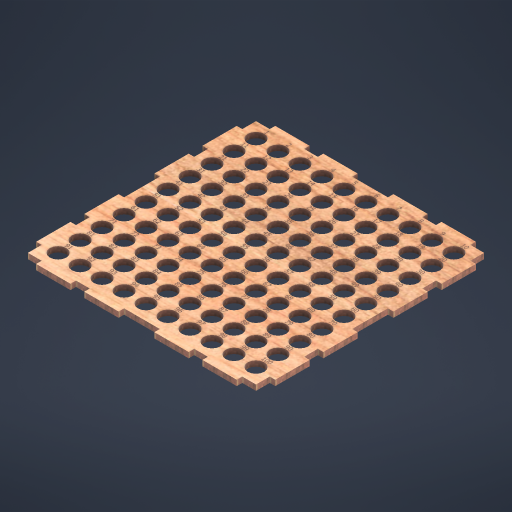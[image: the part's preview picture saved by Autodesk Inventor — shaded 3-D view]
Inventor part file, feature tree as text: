
AUTODESK INVENTOR PART (.ipt)
format: ipt  version: 2024.1 (Build 281209000, 209)  size: 8,317,440 bytes
history: native  units: mm
features: extrude x2, sketch x2, projected_geometry x1
ambient origin geometry x8: Origin, YZ Plane, XZ Plane, XY Plane, X Axis, Y Axis, Z Axis, Center Point
bodies: Solid1 (feature_tree)
feature tree (5):
  extrude  "Extrusion1"  Depth=100.0mm
  extrude  "Extrusion2"  Depth=5.0mm
  sketch  "Sketch1"  dims[d0=12.0mm d1=100.0mm d3=16.0mm]
  sketch  "Sketch2"  dims[d4=100.0mm d6=16.0mm d9=5.0mm d10=5.0mm d11=4.0mm d12=4.0mm d13=10.0mm d14=10.0mm d15=25.0mm d16=4.0mm d17=25.0mm d18=10.0mm d19=25.0mm d20=10.0mm d21=25.0mm d22=4.0mm d23=40.0mm d25=360.0deg d27=4.0mm d28=0.0mm d29=3.0mm d30=0.5mm d31=16.0mm d32=4.0mm d33=3.0mm d34=4.0mm d35=3.0mm d36=4.0mm d37=3.0mm d38=4.0mm d39=3.0mm d40=4.0mm d41=3.0mm d42=4.0mm d43=3.0mm d44=4.0mm d45=3.0mm d46=4.0mm d47=3.0mm d48=4.0mm d49=3.0mm d50=4.0mm d51=3.0mm d52=4.0mm d53=3.0mm d54=4.0mm d55=3.0mm d56=4.0mm d57=3.0mm d58=4.0mm d59=3.0mm d60=4.0mm d61=3.0mm d62=4.0mm d63=3.0mm d64=4.0mm d65=3.0mm d66=4.0mm d67=3.0mm d68=4.0mm d69=3.0mm d70=4.0mm d71=3.0mm d72=4.0mm d73=3.0mm d74=4.0mm d75=3.0mm d76=4.0mm d77=3.0mm d78=4.0mm d79=3.0mm d80=4.0mm d81=3.0mm d82=4.0mm d83=3.0mm d84=4.0mm d85=3.0mm d86=4.0mm d87=3.0mm d88=4.0mm d89=3.0mm d90=4.0mm d91=3.0mm d92=4.0mm d93=3.0mm d94=4.0mm d95=3.0mm d96=4.0mm d97=3.0mm d98=4.0mm d99=3.0mm d100=4.0mm d101=3.0mm d102=4.0mm d103=3.0mm d104=4.0mm d105=3.0mm d106=4.0mm d107=3.0mm d108=4.0mm d109=3.0mm d110=4.0mm d111=3.0mm d112=4.0mm d113=3.0mm d114=4.0mm d115=3.0mm d116=4.0mm d117=3.0mm d118=4.0mm d119=3.0mm d120=4.0mm d121=3.0mm d122=4.0mm d123=3.0mm d124=4.0mm d125=3.0mm d126=4.0mm d127=3.0mm d128=4.0mm d129=3.0mm d130=4.0mm d131=3.0mm d132=4.0mm d133=3.0mm d134=4.0mm d135=3.0mm d136=4.0mm d137=3.0mm d138=4.0mm d139=3.0mm d140=4.0mm d141=3.0mm d142=4.0mm d143=3.0mm d144=4.0mm d145=3.0mm d146=4.0mm d147=3.0mm d148=4.0mm d149=3.0mm d150=4.0mm d151=3.0mm d152=4.0mm d153=3.0mm d154=4.0mm d155=3.0mm d156=4.0mm d157=3.0mm d158=4.0mm d159=3.0mm d160=4.0mm d161=3.0mm d162=4.0mm d163=3.0mm d164=4.0mm d165=3.0mm d166=4.0mm d167=3.0mm d168=4.0mm d169=3.0mm d170=4.0mm d171=3.0mm d172=4.0mm d173=3.0mm d174=4.0mm d175=3.0mm d176=4.0mm d177=3.0mm d178=4.0mm d179=3.0mm d180=4.0mm d181=3.0mm d182=4.0mm d183=3.0mm d184=4.0mm d185=3.0mm d186=4.0mm d187=3.0mm d188=4.0mm d189=3.0mm d190=4.0mm d191=3.0mm d192=4.0mm d193=3.0mm d194=4.0mm d195=3.0mm d196=4.0mm d197=3.0mm d198=4.0mm d199=3.0mm d200=4.0mm d201=3.0mm d202=4.0mm d203=3.0mm d204=4.0mm d205=3.0mm d206=4.0mm d207=3.0mm d208=4.0mm d209=3.0mm d210=4.0mm d211=3.0mm d212=4.0mm d213=3.0mm d214=4.0mm d215=3.0mm d216=4.0mm d217=3.0mm d218=4.0mm d219=3.0mm d220=4.0mm d221=3.0mm d222=4.0mm d223=3.0mm d224=4.0mm d225=3.0mm d226=4.0mm d227=3.0mm d228=4.0mm d229=3.0mm d230=4.0mm d231=0.5mm d232=0.5mm d233=0.5mm d234=0.5mm d235=0.5mm d236=0.5mm d237=0.5mm d238=0.5mm d239=0.5mm d240=1.0mm d241=0.0mm]
  projected_geometry  "Project Cut Edges1"
